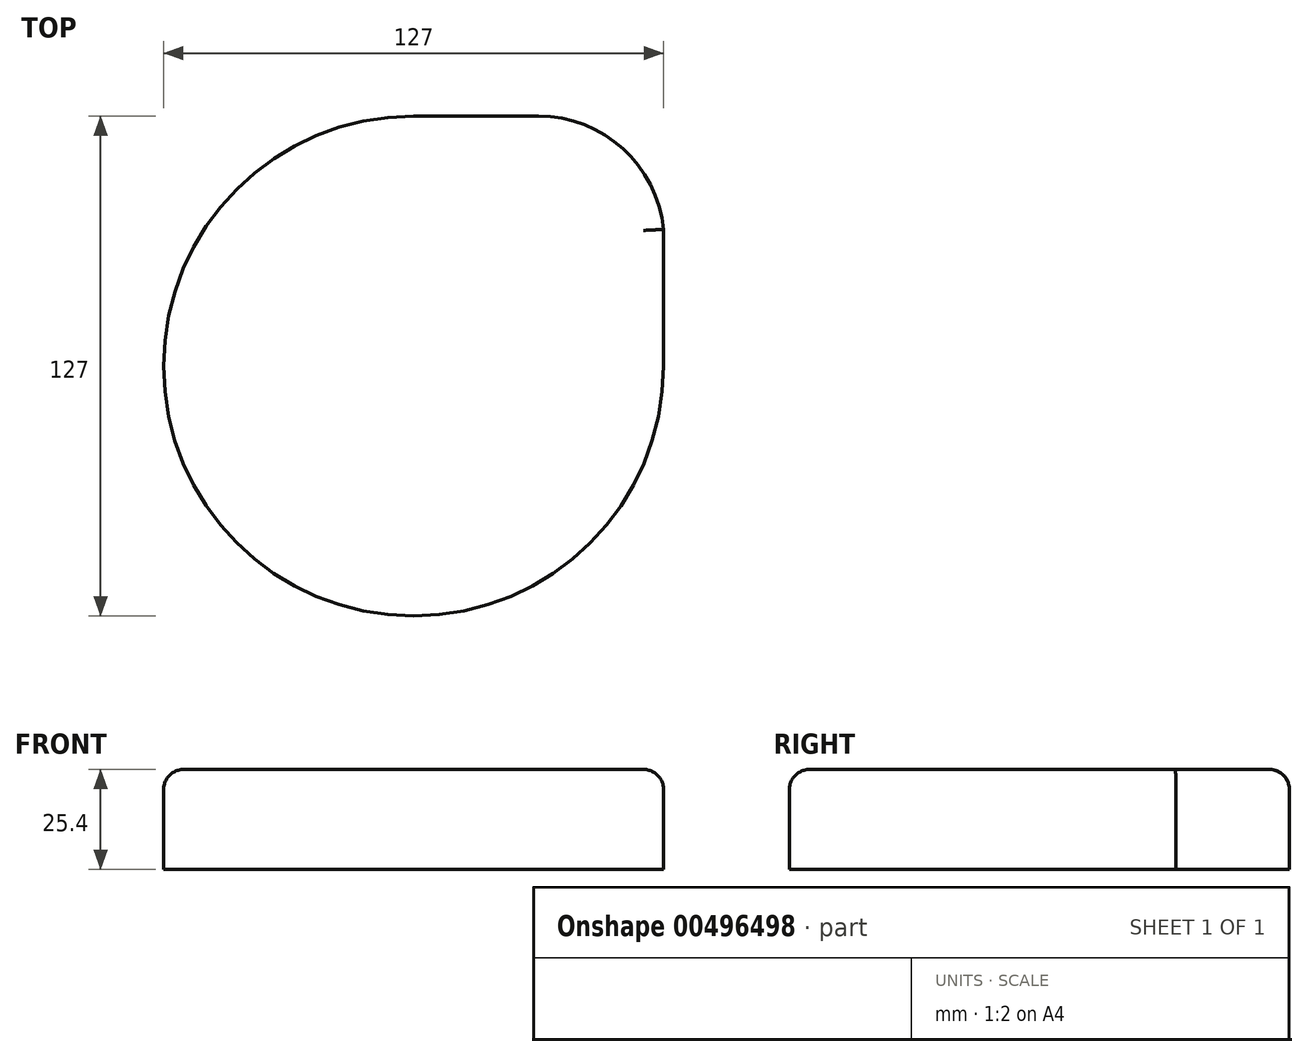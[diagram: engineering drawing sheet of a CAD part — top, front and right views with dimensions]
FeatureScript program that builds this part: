
annotation { "Feature Type Name" : "Feature", "Feature Type Description" : "" }
export const myFeature = defineFeature(function(context is Context, id is Id, definition is map)
    precondition{}
    {
        {
            var Q0;
            Q0=qCreatedBy(makeId("Top.planeOp"),FACE);
            var sketch = newSketch(context, id + "F0", { "sketchPlane" : qUnion([Q0])});
            skArc(sketch, "E0", {"start": v(0, 63.82) * mm, "mid": v(-44.92, -44.57) * mm, "end": v(63.49, 0.3) * mm});
            skLineSegment(sketch, "E1", {"start": v(0, 63.82) * mm, "end": v(31.75, 63.81) * mm});
            skLineSegment(sketch, "E2", {"start": v(63.5, 35.03) * mm, "end": v(63.49, 0) * mm});
            skArc(sketch, "E3", {"start": v(63.5, 35.03) * mm, "mid": v(53.17, 55.55) * mm, "end": v(31.75, 63.81) * mm});
            skPoint(sketch, "E4.orphan", {"position": v(63.5, 63.8) * mm});
            skPoint(sketch, "E5.start.orphan", {"position": v(63.5, 31.9) * mm});
            skSolve(sketch);
        }
        {
            var Q0;
            {var subQ0=sQuery(id+"F0.wireOp",EDGE,"E0");Q0=makeQuery(id+"F0.imprint","IMPRINT",FACE,{"disambiguationData":[TD([[makeQuery(id+"F0.imprint","IMPRINT",EDGE,{"derivedFrom":subQ0}),1.0]])]});}
            extrude(context, id + "F1", {"entities" : qUnion([Q0]), "depth" : 25.4 * mm});
        }
        {
            var Q0;
            Q0=makeQuery(id+"F1.opExtrude","CAP_EDGE",EDGE,{"disambiguationData":[OSD([sQuery(id+"F0.wireOp",EDGE,"E0")])],"isStart":false});
            fillet(context, id + "F2", {"entities" : qUnion([Q0]), "radius" : 5.08 * mm, "tangentPropagation" : true, "allowEdgeOverflow" : false});
        }
    });
